# Revit family: Rotor Falvon 6504 Series - 6504PCSSNP
name_source: partatom
category: Acessórios do tubo
units: mm (PartAtom-declared; Revit-internal decimal feet)

## family parameters
Com base no plano de trabalho = Não
Compartilhado = Não
Corte com vazios quando carregada = Não
Cota do conector redondo = Utilizar diâmetro
Número OmniClass = 23.60.30.11.14
Sempre na vertical = Sim
Tipo de parte = Normal
Título OmniClass = Pipework Fittings

## types (8) — shared parameters
Angle = 25.00°
Black Plastic = Black Plastic
Blue = Blue Plastic
Body height = 1 '
Descrição = FALCON 6504-PC-SS-NP Rotor
Fabricante = Rain Bird
Modelo = 6504-PCSSNP
RainBird: Code = B65521NP
RainBird: Description = FALCON 6504-PC-SS-NP Rotor
RainBird: Product Link = https://www.rainbird.com
Side inlet = Não
SupportProjetos: Level of Detail = LOD 300
SupportProjetos: Reviw = R00
TABLE 30 = TABLE 30psi
TABLE 40 = TABLE 40psi
TABLE 50 = TABLE 50psi
TABLE 60 = TABLE 60psi
TABLE 70 = TABLE 70psi
TABLE 80 = TABLE 80psi
TABLE 90 = TABLE 90psi
URL = https://www.rainbird.com
Water = Water
zero-valued in all types: Conection, DD1, DD10, DD11, DD12, DD13, DD3, DD4, DD5, DD7, Elevação padrão, H1, Pop up height, R1, R2, R3, R4, R5, RN, RT

## per-type parameters (varying)
| type | Instance |
| Nozzle 4 | 1 ' |
| Nozzle 6 | 2 ' |
| Nozzle 8 | 3 ' |
| Nozzle 10 | 4 ' |
| Nozzle 12 | 5 ' |
| Tipo 14 | 6 ' |
| Nozzle 16 | 7 ' |
| Nozzle 18 | 8 ' |
